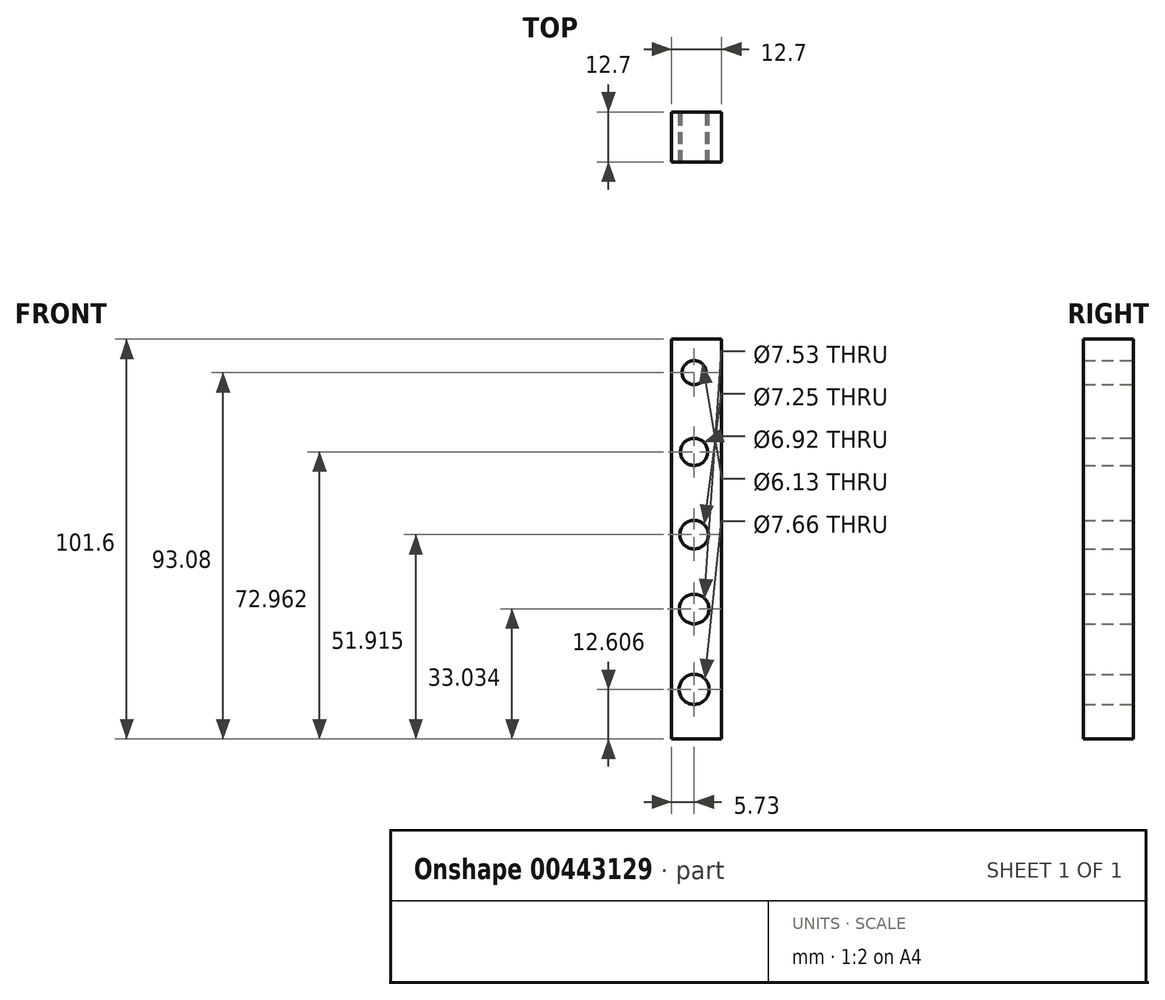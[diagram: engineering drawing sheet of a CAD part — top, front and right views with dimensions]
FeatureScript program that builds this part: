
annotation { "Feature Type Name" : "Feature", "Feature Type Description" : "" }
export const myFeature = defineFeature(function(context is Context, id is Id, definition is map)
    precondition{}
    {
        {
            var Q0;
            Q0=qCreatedBy(makeId("Front.planeOp"),FACE);
            var sketch = newSketch(context, id + "F0", { "sketchPlane" : qUnion([Q0])});
            skLineSegment(sketch, "E0", {"start": v(-44.42, 37.15) * mm, "end": v(-31.72, 37.15) * mm});
            skLineSegment(sketch, "E1", {"start": v(-31.72, 37.15) * mm, "end": v(-31.72, -64.45) * mm});
            skLineSegment(sketch, "E2", {"start": v(-31.72, -64.45) * mm, "end": v(-44.42, -64.45) * mm});
            skLineSegment(sketch, "E3", {"start": v(-44.42, -64.45) * mm, "end": v(-44.42, 37.15) * mm});
            skCircle(sketch, "E4", {"center": v(-38.69, 28.63) * mm, "radius": 3.06 * mm});
            skCircle(sketch, "E5", {"center": v(-38.69, 8.51) * mm, "radius": 3.46 * mm});
            skCircle(sketch, "E6", {"center": v(-38.69, -12.54) * mm, "radius": 3.62 * mm});
            skCircle(sketch, "E7", {"center": v(-38.69, -31.42) * mm, "radius": 3.77 * mm});
            skCircle(sketch, "E8", {"center": v(-38.69, -51.84) * mm, "radius": 3.83 * mm});
            skSolve(sketch);
        }
        {
            var Q0;
            Q0 = qSketchRegion(id + "F0", true);
            extrude(context, id + "F1", {"entities" : qUnion([Q0]), "depth" : 12.7 * mm});
        }
    });
